# Revit family: 02 DG 980-780
name_source: partatom
category: Air Terminals
revit_build: Autodesk Revit 2017 (Build: 20160225_1515(x64)
units: mm (PartAtom-declared; Revit-internal decimal feet)

## family parameters
Always vertical = Yes
Cut with Voids When Loaded = No
Host = Wall
Part Type = Normal
Room Calculation Point = No
Round Connector Dimension = Use Diameter
Shared = No

## types (2) — shared parameters
Acabado_Campana = Teka_Acero Inoxidable Satinado
Ca_1_Frecuencia 50/60 Hz = Yes
Ca_1_Opción de recirculación = Yes
Ca_1_Potencia Iluminación, W. (Led) = 2 x 3W
Ca_1_Potencia motor, W. = 230
Ca_1_Potencia máxima, W. = 270
Ca_1_Salida exterior, mm. = 150
Ca_1_Tensión 220/240 V. = Sí
Ca_2_Electrónico = Yes
Ca_2_Pulsante (Retroiluminación) = No
Ca_2_Touch Control = No
Ca_3_Filtro metálico decorativo = Yes
Ca_3_Indicador de saturación de filtros = No
Ca_3_Motor Blindado = Yes
Ca_3_N° de Velocidades = 3 +1
Ca_3_N° de motores = 1 DT
Ca_3_Panel de fácil limpieza = No
Ca_3_Piloto de funcionamiento = Yes
Ca_3_Programación de tiempo de aspiración = Yes
Ca_3_Sensor de humedad = No
Ca_4_Ala de Cristal = Yes
Ca_4_Ala de acero Inoxidable = No
Ca_4_Fabricada en Acero Austenítico Certificado = Yes
Ca_Alto = 625 mm
Ca_Creado por = Catálogo Arquitectura
Ca_Código Catálogo Arquitectura = 465_TEK_037
Ca_Código EAN = 8421152130384
Ca_Fabricante = Teka
Ca_Instalación = Mural
Ca_Itemizado CDT = E 08 06 02
Ca_Masterformat = 11 30 13.13
Ca_Material Principal = Acero Austenítico Certificado
Ca_Medidas de embalaje = 59 x 39,5 x 98,1
Ca_País de Fabricación = España
Ca_Peso = 15,3 kg
Ca_Profundidad = 500 mm  [stored 1.64042 ft]
Ca_Representante = Teka
Ca_Teléfono = 99821 1017
Ca_Usos = Campana de extracción y recirculación de cocina
Ca_Web del Fabricante = www.teka.com
Ca_Web del Representante = www.teka.cl
Description = Campana de extracción y recirculación de cocina (NO incluye filtros de Carbón)
Manufacturer = Teka
Model = DG 980-780 Cristal Ultra Slim
URL = www.teka.cl
Vidrio Templado = Teka_Vidrio

## per-type parameters (varying)
| type | Alto | Ca_Ancho | Ca_Código del Producto | Ca_Especificaciones Técnicas | Ca_Producto | Control_Alto | Longitud |
| DG 780 Cristal Ultra Slim | 955 mm | 700 mm | 40485351 | Campana decorativa modelo mural DG 780 Cristal Ultra Slim | Campana mural DG 780 Cristal Ultra Slim | 955 mm | 700 mm |
| DG 980 Cristal Ultra Slim | 926 mm | 900 mm  [stored 2.95276 ft] | 40485352 | Campana decorativa modelo mural DG 980 Cristal Ultra Slim | Campana mural DG 980 Cristal Ultra Slim | 926 mm | 900 mm  [stored 2.95276 ft] |

note: [stored X ft] marks values corroborated as IEEE doubles in the binary element streams (Revit-internal decimal feet)

## geometry (parser evidence)
native form markers: Sweep x3
no freeform markers — native parametric forms only
